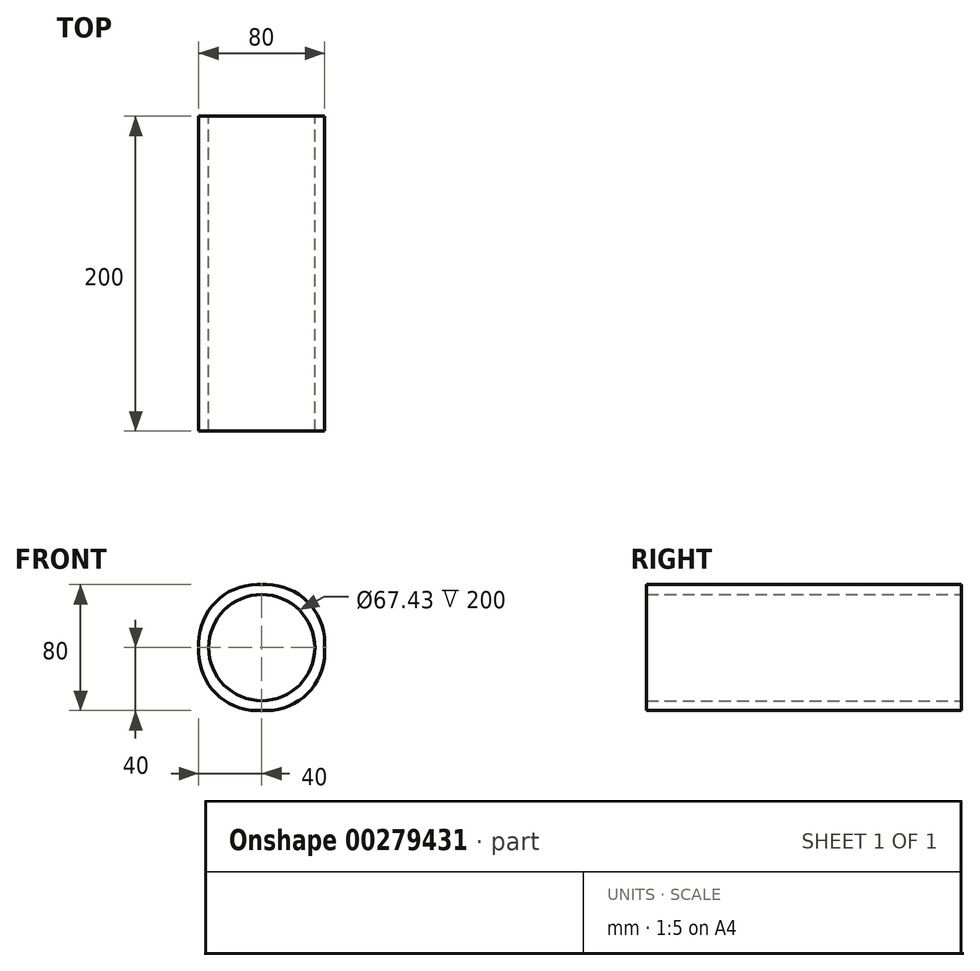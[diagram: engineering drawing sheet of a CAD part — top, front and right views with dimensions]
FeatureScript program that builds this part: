
annotation { "Feature Type Name" : "Feature", "Feature Type Description" : "" }
export const myFeature = defineFeature(function(context is Context, id is Id, definition is map)
    precondition{}
    {
        {
            var Q0;
            Q0=qCreatedBy(makeId("Front.planeOp"),FACE);
            var sketch = newSketch(context, id + "F0", { "sketchPlane" : qUnion([Q0])});
            skLineSegment(sketch, "E0.top", {"start": v(-3, -40) * mm, "end": v(3, -40) * mm});
            skLineSegment(sketch, "E0.left", {"start": v(-40, 3) * mm, "end": v(-40, -3) * mm});
            skLineSegment(sketch, "E0.right", {"start": v(40, 3) * mm, "end": v(40, -3) * mm});
            skCircle(sketch, "E1", {"center": v(0, 0) * mm, "radius": 33.72 * mm});
            skPoint(sketch, "E2.visualSharp", {"position": v(-40, 40) * mm});
            skArc(sketch, "E2.filletArc", {"start": v(-3, 40) * mm, "mid": v(-29.16, 29.16) * mm, "end": v(-40, 3) * mm});
            skPoint(sketch, "E3.visualSharp", {"position": v(-40, -40) * mm});
            skArc(sketch, "E3.filletArc", {"start": v(-40, -3) * mm, "mid": v(-29.16, -29.16) * mm, "end": v(-3, -40) * mm});
            skPoint(sketch, "E4.visualSharp", {"position": v(40, -40) * mm});
            skArc(sketch, "E4.filletArc", {"start": v(3, -40) * mm, "mid": v(29.16, -29.16) * mm, "end": v(40, -3) * mm});
            skPoint(sketch, "E5.visualSharp", {"position": v(40, 40) * mm});
            skArc(sketch, "E5.filletArc", {"start": v(40, 3) * mm, "mid": v(29.16, 29.16) * mm, "end": v(3, 40) * mm});
            skPoint(sketch, "E0.bottom.end.orphan", {"position": v(0, 40) * mm});
            skLineSegment(sketch, "E6", {"start": v(-3, 40) * mm, "end": v(3, 40) * mm});
            skPoint(sketch, "E7.end.orphan", {"position": v(0, 33.72) * mm});
            skPoint(sketch, "E8.orphan", {"position": v(-75.02, 3) * mm});
            skSolve(sketch);
        }
        {
            var Q0;
            Q0=makeQuery(id+"F0.imprint","IMPRINT",FACE,{"disambiguationData":[TD([[makeQuery(id+"F0.imprint","IMPRINT",EDGE,{"derivedFrom":sQuery(id+"F0.wireOp",EDGE,"E0.top")}),1.0]])]});
            extrude(context, id + "F1", {"entities" : qUnion([Q0]), "depth" : 200 * mm});
        }
    });
